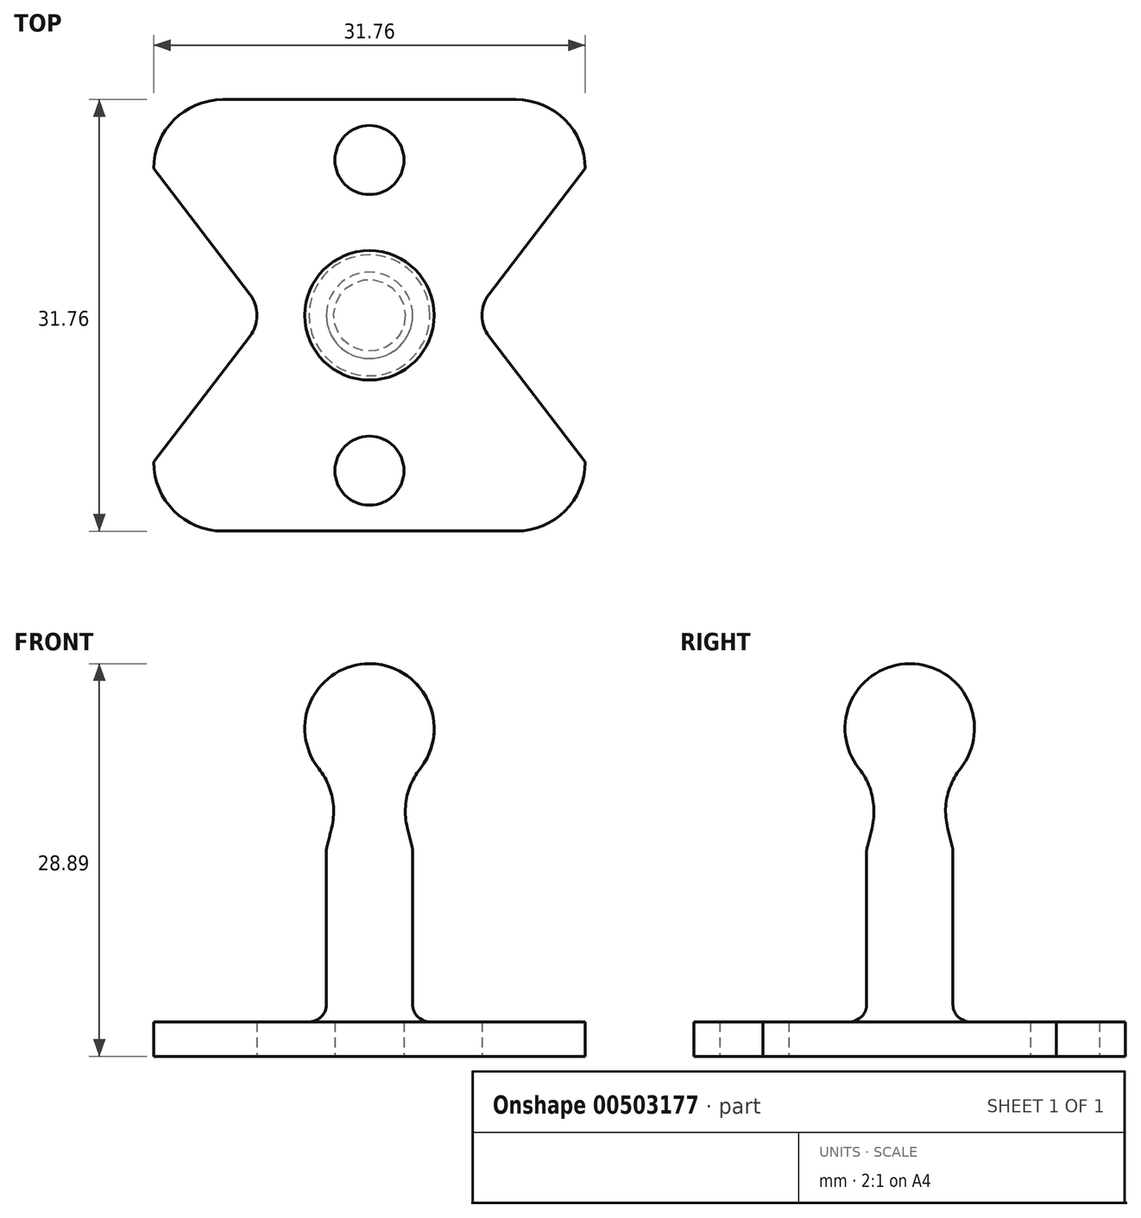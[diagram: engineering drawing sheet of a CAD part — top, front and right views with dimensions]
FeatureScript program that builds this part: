
annotation { "Feature Type Name" : "Feature", "Feature Type Description" : "" }
export const myFeature = defineFeature(function(context is Context, id is Id, definition is map)
    precondition{}
    {
        {
            var Q0;
            Q0=qCreatedBy(makeId("Front.planeOp"),FACE);
            var sketch = newSketch(context, id + "F0", { "sketchPlane" : qUnion([Q0])});
            skLineSegment(sketch, "E0.bottom", {"start": v(0, 0) * mm, "end": v(3.17, 0) * mm});
            skLineSegment(sketch, "E0.left", {"start": v(0, 0) * mm, "end": v(0, 12.7) * mm});
            skLineSegment(sketch, "E0.right", {"start": v(3.17, 1.27) * mm, "end": v(3.17, 12.7) * mm});
            skLineSegment(sketch, "E1.left", {"start": v(0, 12.7) * mm, "end": v(0, 16.83) * mm});
            skLineSegment(sketch, "E1.right", {"start": v(2.03, 17.28) * mm, "end": v(2.03, 17.28) * mm});
            skArc(sketch, "E2", {"start": v(2.03, 17.28) * mm, "mid": v(4.65, 22.63) * mm, "end": v(0, 26.35) * mm});
            skLineSegment(sketch, "E3", {"start": v(0, 16.83) * mm, "end": v(0, 26.35) * mm});
            skLineSegment(sketch, "E4", {"start": v(4.44, 0) * mm, "end": v(4.45, 0) * mm});
            skPoint(sketch, "E5.visualSharp", {"position": v(3.17, 0) * mm});
            skArc(sketch, "E5.filletArc", {"start": v(3.17, 1.27) * mm, "mid": v(3.55, 0.37) * mm, "end": v(4.44, 0) * mm});
            skLineSegment(sketch, "E6", {"start": v(3.17, 0) * mm, "end": v(4.44, 0) * mm});
            skLineSegment(sketch, "E7", {"start": v(2.03, 17.28) * mm, "end": v(3.18, 12.7) * mm});
            skSolve(sketch);
        }
        {
            var Q0;
            Q0=makeQuery(id+"F0.imprint","IMPRINT",FACE,{"disambiguationData":[TD([[makeQuery(id+"F0.imprint","IMPRINT",EDGE,{"derivedFrom":sQuery(id+"F0.wireOp",EDGE,"E0.bottom")}),1.0]])]});
            var Q1;
            Q1=sQuery(id+"F0.wireOp",EDGE,"E3");
            revolve(context, id + "F1", {"entities" : qUnion([Q0]), "axis" : qUnion([Q1]), "revolveType" : RevolveType.FULL});
        }
        {
            var Q0;
            Q0=makeQuery(id+"F1.opRevolve","SWEPT_FACE",FACE,{"disambiguationData":[OSD([sQuery(id+"F0.wireOp",EDGE,"E0.bottom")])]});
            var sketch = newSketch(context, id + "F2", { "sketchPlane" : qUnion([Q0])});
            skLineSegment(sketch, "E8.bottom", {"start": v(-15.88, 15.87) * mm, "end": v(15.88, 15.88) * mm});
            skLineSegment(sketch, "E8.top", {"start": v(-15.88, -15.88) * mm, "end": v(15.88, -15.88) * mm});
            skLineSegment(sketch, "E8.left", {"start": v(-15.88, 15.87) * mm, "end": v(-15.88, -15.88) * mm});
            skLineSegment(sketch, "E8.right", {"start": v(15.88, 15.88) * mm, "end": v(15.88, -15.88) * mm});
            skSolve(sketch);
        }
        {
            var Q0;
            Q0=makeQuery(id+"F2.imprint","IMPRINT",FACE,{"disambiguationData":[TD([[makeQuery(id+"F2.imprint","IMPRINT",EDGE,{"derivedFrom":sQuery(id+"F2.wireOp",EDGE,"E8.bottom")}),-1.0]])]});
            var Q1;
            Q1=makeQuery(id+"F2.imprint","IMPRINT",FACE,{"disambiguationData":[TD([[makeQuery(id+"F2.imprint","IMPRINT",EDGE,{"derivedFrom":makeQuery(id+"F1.opRevolve","SWEPT_EDGE",EDGE,{"disambiguationData":[OSD([sQuery(id+"F0.wireOp",EDGE,"E0.bottom"),sQuery(id+"F0.wireOp",EDGE,"E0.right")])]})}),1.0]])]});
            var Q2;
            Q2=makeQuery(id+"F2.imprint","IMPRINT",FACE,{"disambiguationData":[TD([[makeQuery(id+"F2.imprint","IMPRINT",EDGE,{"derivedFrom":makeQuery(id+"F1.opRevolve","SWEPT_EDGE",EDGE,{"disambiguationData":[OSD([sQuery(id+"F0.wireOp",EDGE,"E5.filletArc"),sQuery(id+"F0.wireOp",EDGE,"E6")])]})}),1.0]])]});
            extrude(context, id + "F3", {"entities" : qUnion([Q0, Q1, Q2]), "depth" : 2.54 * mm});
        }
        {
            var Q0;
            Q0=makeQuery(id+"F3.opExtrude","SWEPT_EDGE",EDGE,{"disambiguationData":[OSD([sQuery(id+"F2.wireOp",EDGE,"E8.bottom"),sQuery(id+"F2.wireOp",EDGE,"E8.left")])]});
            var Q1;
            Q1=makeQuery(id+"F3.opExtrude","SWEPT_EDGE",EDGE,{"disambiguationData":[OSD([sQuery(id+"F2.wireOp",EDGE,"E8.bottom"),sQuery(id+"F2.wireOp",EDGE,"E8.right")])]});
            var Q2;
            Q2=makeQuery(id+"F3.opExtrude","SWEPT_EDGE",EDGE,{"disambiguationData":[OSD([sQuery(id+"F2.wireOp",EDGE,"E8.top"),sQuery(id+"F2.wireOp",EDGE,"E8.right")])]});
            var Q3;
            Q3=makeQuery(id+"F3.opExtrude","SWEPT_EDGE",EDGE,{"disambiguationData":[OSD([sQuery(id+"F2.wireOp",EDGE,"E8.top"),sQuery(id+"F2.wireOp",EDGE,"E8.left")])]});
            fillet(context, id + "F4", {"entities" : qUnion([Q0, Q1, Q2, Q3]), "radius" : 5.08 * mm, "tangentPropagation" : true, "allowEdgeOverflow" : false});
        }
        {
            var Q0;
            Q0=makeQuery(id+"F3.opExtrude","CAP_FACE",FACE,{"disambiguationData":[OSD([sQuery(id+"F0.wireOp",EDGE,"E0.bottom"),sQuery(id+"F0.wireOp",EDGE,"E0.right"),sQuery(id+"F2.wireOp",EDGE,"E8.bottom"),sQuery(id+"F2.wireOp",EDGE,"E8.top"),sQuery(id+"F2.wireOp",EDGE,"E8.left"),sQuery(id+"F2.wireOp",EDGE,"E8.right")])],"isStart":false});
            var sketch = newSketch(context, id + "F5", { "sketchPlane" : qUnion([Q0])});
            skCircle(sketch, "E9", {"center": v(0, 11.43) * mm, "radius": 2.54 * mm});
            skCircle(sketch, "E10", {"center": v(0, -11.43) * mm, "radius": 2.54 * mm});
            skSolve(sketch);
        }
        {
            var Q0;
            Q0=makeQuery(id+"F5.imprint","IMPRINT",FACE,{"disambiguationData":[TD([[makeQuery(id+"F5.imprint","IMPRINT",EDGE,{"derivedFrom":sQuery(id+"F5.wireOp",EDGE,"E9")}),1.0]])]});
            var Q1;
            Q1=makeQuery(id+"F5.imprint","IMPRINT",FACE,{"disambiguationData":[TD([[makeQuery(id+"F5.imprint","IMPRINT",EDGE,{"derivedFrom":sQuery(id+"F5.wireOp",EDGE,"E10")}),1.0]])]});
            extrude(context, id + "F6", {"entities" : qUnion([Q0, Q1]), "operationType" : NewBodyOperationType.REMOVE, "endBound" : BoundingType.THROUGH_ALL, "oppositeDirection" : true, "depth" : 25.4 * mm});
        }
        {
            var Q0;
            Q0=makeQuery(id+"F1.opRevolve","SWEPT_EDGE",EDGE,{"disambiguationData":[OSD([sQuery(id+"F0.wireOp",EDGE,"E0.top"),sQuery(id+"F0.wireOp",EDGE,"E0.right")])]});
            fillet(context, id + "F7", {"entities" : qUnion([Q0]), "radius" : 1.27 * mm, "tangentPropagation" : true, "allowEdgeOverflow" : false});
        }
        {
            var Q0;
            Q0=makeQuery(id+"F3.opExtrude","CAP_FACE",FACE,{"disambiguationData":[OSD([sQuery(id+"F2.wireOp",EDGE,"E8.bottom"),sQuery(id+"F2.wireOp",EDGE,"E8.top"),sQuery(id+"F2.wireOp",EDGE,"E8.left"),sQuery(id+"F2.wireOp",EDGE,"E8.right")])],"isStart":false});
            var sketch = newSketch(context, id + "F8", { "sketchPlane" : qUnion([Q0])});
            skLineSegment(sketch, "E11", {"start": v(-15.88, 10.8) * mm, "end": v(-8.8, 1.54) * mm});
            skLineSegment(sketch, "E12", {"start": v(-8.8, -1.54) * mm, "end": v(-15.88, -10.8) * mm});
            skLineSegment(sketch, "E13", {"start": v(15.88, 10.8) * mm, "end": v(8.8, 1.54) * mm});
            skLineSegment(sketch, "E14", {"start": v(8.8, -1.54) * mm, "end": v(15.88, -10.8) * mm});
            skLineSegment(sketch, "E15", {"start": v(15.88, -10.8) * mm, "end": v(15.88, 10.8) * mm});
            skLineSegment(sketch, "E16", {"start": v(-15.88, 10.8) * mm, "end": v(-15.88, -10.8) * mm});
            skPoint(sketch, "E17.visualSharp", {"position": v(-7.62, 0) * mm});
            skArc(sketch, "E17.filletArc", {"start": v(-8.8, -1.54) * mm, "mid": v(-8.28, 0) * mm, "end": v(-8.8, 1.54) * mm});
            skPoint(sketch, "E18.visualSharp", {"position": v(7.62, 0) * mm});
            skArc(sketch, "E18.filletArc", {"start": v(8.8, 1.54) * mm, "mid": v(8.28, 0) * mm, "end": v(8.8, -1.54) * mm});
            skSolve(sketch);
        }
        {
            var Q0;
            Q0=makeQuery(id+"F8.imprint","IMPRINT",FACE,{"disambiguationData":[TD([[makeQuery(id+"F8.imprint","IMPRINT",EDGE,{"derivedFrom":sQuery(id+"F8.wireOp",EDGE,"E11")}),-1.0]])]});
            var Q1;
            Q1=makeQuery(id+"F8.imprint","IMPRINT",FACE,{"disambiguationData":[TD([[makeQuery(id+"F8.imprint","IMPRINT",EDGE,{"derivedFrom":sQuery(id+"F8.wireOp",EDGE,"E13")}),1.0]])]});
            extrude(context, id + "F9", {"entities" : qUnion([Q0, Q1]), "operationType" : NewBodyOperationType.REMOVE, "endBound" : BoundingType.THROUGH_ALL, "oppositeDirection" : true, "depth" : 25.4 * mm});
        }
        {
            var Q0;
            Q0=makeQuery(id+"F1.opRevolve","SWEPT_EDGE",EDGE,{"disambiguationData":[OSD([sQuery(id+"F0.wireOp",EDGE,"E2"),sQuery(id+"F0.wireOp",EDGE,"E7")])]});
            fillet(context, id + "F10", {"entities" : qUnion([Q0]), "radius" : 5.08 * mm, "tangentPropagation" : true, "allowEdgeOverflow" : false});
        }
    });
